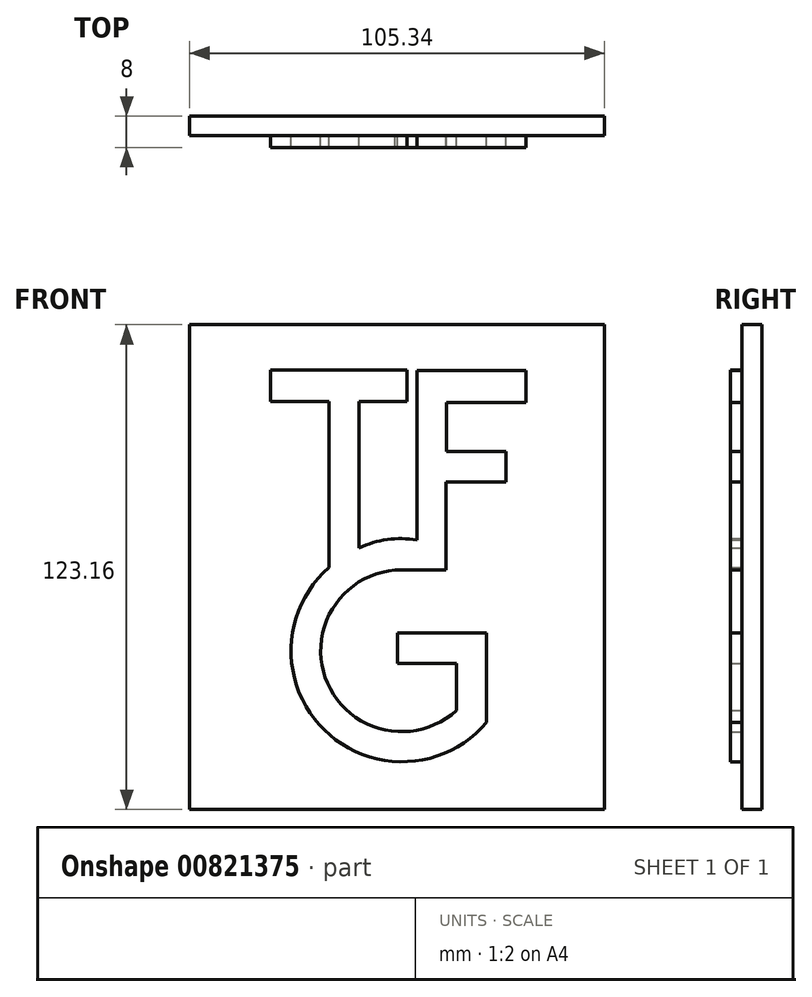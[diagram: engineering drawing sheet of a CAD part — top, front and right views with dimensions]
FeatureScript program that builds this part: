
annotation { "Feature Type Name" : "Feature", "Feature Type Description" : "" }
export const myFeature = defineFeature(function(context is Context, id is Id, definition is map)
    precondition{}
    {
        {
            var Q0;
            Q0=qCreatedBy(makeId("Front.planeOp"),FACE);
            var sketch = newSketch(context, id + "F0", { "sketchPlane" : qUnion([Q0])});
            skLineSegment(sketch, "E0", {"start": v(-37.59, 36.76) * mm, "end": v(-37.59, 28.75) * mm});
            skLineSegment(sketch, "E1", {"start": v(-37.59, 28.75) * mm, "end": v(-22.74, 28.75) * mm});
            skLineSegment(sketch, "E2", {"start": v(-22.74, 28.75) * mm, "end": v(-22.74, -13.42) * mm});
            skLineSegment(sketch, "E3", {"start": v(-37.59, 36.76) * mm, "end": v(-2.87, 36.76) * mm});
            skLineSegment(sketch, "E4", {"start": v(-2.87, 36.76) * mm, "end": v(-2.87, 28.74) * mm});
            skLineSegment(sketch, "E5", {"start": v(-2.87, 28.74) * mm, "end": v(-15.04, 28.74) * mm});
            skLineSegment(sketch, "E6", {"start": v(-15.04, 28.74) * mm, "end": v(-15.04, -8.42) * mm});
            skArc(sketch, "E7", {"start": v(-0.4, -6.42) * mm, "mid": v(-7.87, -6.29) * mm, "end": v(-15.04, -8.42) * mm});
            skLineSegment(sketch, "E8", {"start": v(-0.4, -6.42) * mm, "end": v(-0.4, 36.7) * mm});
            skLineSegment(sketch, "E9", {"start": v(-0.4, 36.7) * mm, "end": v(27.35, 36.7) * mm});
            skLineSegment(sketch, "E10", {"start": v(27.35, 36.7) * mm, "end": v(27.35, 28.53) * mm});
            skLineSegment(sketch, "E11", {"start": v(27.35, 28.53) * mm, "end": v(7.15, 28.53) * mm});
            skLineSegment(sketch, "E12", {"start": v(7.15, 28.53) * mm, "end": v(7.15, 16.08) * mm});
            skLineSegment(sketch, "E13", {"start": v(7.15, 16.08) * mm, "end": v(22.23, 16.08) * mm});
            skLineSegment(sketch, "E14", {"start": v(22.23, 16.08) * mm, "end": v(22.23, 8.33) * mm});
            skLineSegment(sketch, "E15", {"start": v(22.23, 8.33) * mm, "end": v(7.02, 8.33) * mm});
            skLineSegment(sketch, "E16", {"start": v(7.02, 8.33) * mm, "end": v(7.02, -14.04) * mm});
            skLineSegment(sketch, "E17", {"start": v(7.02, -14.04) * mm, "end": v(-5.94, -14.04) * mm});
            skArc(sketch, "E18", {"start": v(-22.74, -13.42) * mm, "mid": v(-23.88, -54.7) * mm, "end": v(17.37, -52.73) * mm});
            skLineSegment(sketch, "E19", {"start": v(17.37, -52.73) * mm, "end": v(17.37, -30.02) * mm});
            skLineSegment(sketch, "E20", {"start": v(17.37, -30.02) * mm, "end": v(-5.27, -30.02) * mm});
            skLineSegment(sketch, "E21", {"start": v(-5.27, -30.02) * mm, "end": v(-5.27, -37.8) * mm});
            skLineSegment(sketch, "E22", {"start": v(-5.27, -37.8) * mm, "end": v(9.65, -37.8) * mm});
            skLineSegment(sketch, "E23", {"start": v(9.65, -37.8) * mm, "end": v(9.65, -49.7) * mm});
            skArc(sketch, "E24", {"start": v(-5.94, -14.04) * mm, "mid": v(-23.07, -42.77) * mm, "end": v(9.65, -49.7) * mm});
            skLineSegment(sketch, "E25.bottom", {"start": v(-58.1, 48.31) * mm, "end": v(47.25, 48.31) * mm});
            skLineSegment(sketch, "E25.top", {"start": v(-58.1, -74.85) * mm, "end": v(47.25, -74.85) * mm});
            skLineSegment(sketch, "E25.left", {"start": v(-58.1, 48.31) * mm, "end": v(-58.1, -74.85) * mm});
            skLineSegment(sketch, "E25.right", {"start": v(47.25, 48.31) * mm, "end": v(47.25, -74.85) * mm});
            skSolve(sketch);
        }
        {
            var Q0;
            Q0=makeQuery(id+"F0.imprint","IMPRINT",FACE,{"disambiguationData":[TD([[makeQuery(id+"F0.imprint","IMPRINT",EDGE,{"derivedFrom":sQuery(id+"F0.wireOp",EDGE,"E0")}),1.0]])]});
            extrude(context, id + "F1", {"entities" : qUnion([Q0]), "depth" : 8 * mm, "offsetDistance" : 25 * mm});
        }
        {
            var Q0;
            Q0 = qSketchRegion(id + "F0", true);
            extrude(context, id + "F2", {"entities" : qUnion([Q0]), "operationType" : NewBodyOperationType.ADD, "depth" : 5 * mm, "offsetDistance" : 25 * mm});
        }
    });
